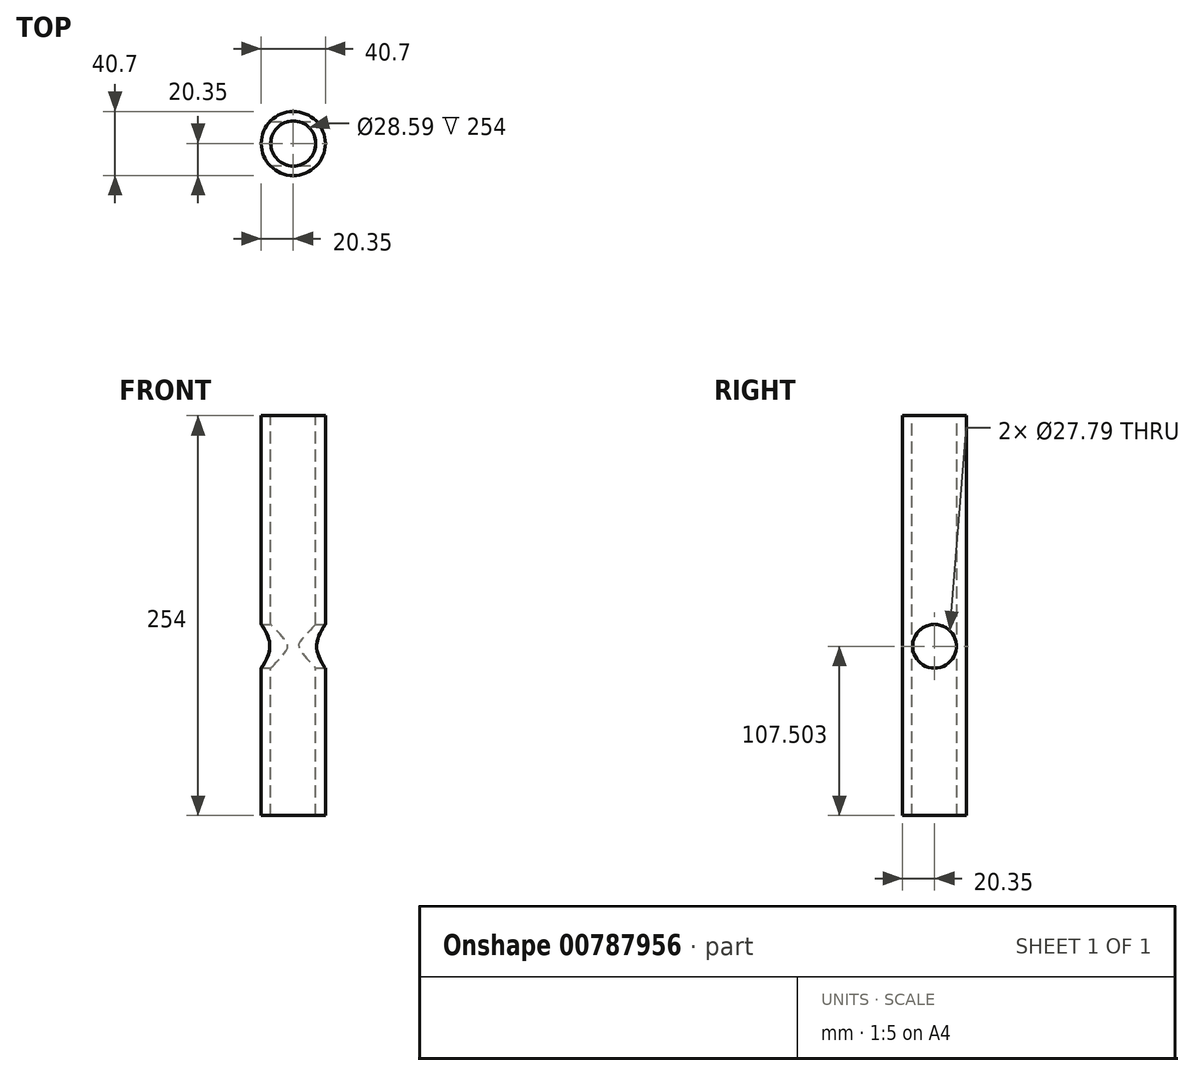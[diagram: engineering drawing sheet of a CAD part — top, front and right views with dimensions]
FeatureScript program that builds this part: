
annotation { "Feature Type Name" : "Feature", "Feature Type Description" : "" }
export const myFeature = defineFeature(function(context is Context, id is Id, definition is map)
    precondition{}
    {
        {
            var Q0;
            Q0=qCreatedBy(makeId("Top.planeOp"),FACE);
            var sketch = newSketch(context, id + "F0", { "sketchPlane" : qUnion([Q0])});
            skCircle(sketch, "E0", {"center": v(0, 0) * mm, "radius": 20.35 * mm});
            skSolve(sketch);
        }
        {
            var Q0;
            Q0 = qSketchRegion(id + "F0", true);
            extrude(context, id + "F1", {"entities" : qUnion([Q0]), "depth" : 254 * mm, "offsetDistance" : 25.4 * mm});
        }
        {
            var Q0;
            Q0=makeQuery(id+"F1.opExtrude","CAP_FACE",FACE,{"disambiguationData":[OSD([sQuery(id+"F0.wireOp",EDGE,"E0")])],"isStart":false});
            var sketch = newSketch(context, id + "F2", { "sketchPlane" : qUnion([Q0])});
            skCircle(sketch, "E1", {"center": v(0, 0) * mm, "radius": 14.3 * mm});
            skSolve(sketch);
        }
        {
            var Q0;
            Q0 = qSketchRegion(id + "F2", true);
            extrude(context, id + "F3", {"entities" : qUnion([Q0]), "operationType" : NewBodyOperationType.REMOVE, "endBound" : BoundingType.THROUGH_ALL, "oppositeDirection" : true, "depth" : 25.4 * mm, "offsetDistance" : 25.4 * mm});
        }
        {
            var Q0;
            Q0=qCreatedBy(makeId("Right.planeOp"),FACE);
            var sketch = newSketch(context, id + "F4", { "sketchPlane" : qUnion([Q0])});
            skCircle(sketch, "E2", {"center": v(0, 107.5) * mm, "radius": 13.9 * mm});
            skSolve(sketch);
        }
        {
            var Q0;
            Q0 = qSketchRegion(id + "F4", true);
            extrude(context, id + "F5", {"entities" : qUnion([Q0]), "operationType" : NewBodyOperationType.REMOVE, "endBound" : BoundingType.THROUGH_ALL, "oppositeDirection" : true, "depth" : 25.4 * mm, "offsetDistance" : 25.4 * mm, "hasSecondDirection" : true, "secondDirectionOppositeDirection" : false, "secondDirectionDepth" : 25.4 * mm});
        }
    });
